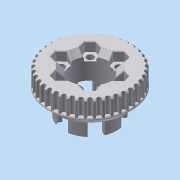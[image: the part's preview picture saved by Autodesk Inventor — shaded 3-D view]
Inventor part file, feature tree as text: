
AUTODESK INVENTOR PART (.ipt)
format: ipt  version: 2014 SP1 (Build 180222100, 222)  size: 2,198,528 bytes
history: native  units: in
note: dims shown in document units (in); Inventor stores cm internally (conversion verified against a paired STEP export)
features: extrude x7, other x4, sketch x4, fillet x4, chamfer x3, projected_geometry x2, move_body x1
ambient origin geometry x8: Origin, YZ Plane, XZ Plane, XY Plane, X Axis, Y Axis, Z Axis, Center Point
bodies: Solid1 (feature_tree), Solid3 (feature_tree)
feature tree (25):
  other  "wheelinsertsketch.ipt"
  other  "40t_pulley.ipt"
  extrude  "Extrusion1"  Depth=0.5in TaperAngle=0.0deg
  extrude  "Extrusion2"  Depth=0.3in TaperAngle=0.0deg
  chamfer  "Chamfer1"  Distance=0.25in Angle=45.0deg
  sketch  "Sketch14"  dims[d39=1.1in d40=0.4724in d41=0.0in d42=5.0in d43=0.0in d44=0.05in d45=0.02in d46=0.125in d61=0.1625in d62=0.125in d63=45.0deg d80=0.38in d81=2.3622in d83=360.0deg d85=1.0in d86=0.0in d87=0.2756in d88=0.0in d90=0.4724in d91=0.0in d92=0.0591in d93=0.125in d94=45.0deg d96=0.0394in d102=0.205in d103=0.0787in]
  move_body  "Move Body2"
  extrude  "Extrusion14"  TaperAngle=90.0deg  [1 undecoded]
  chamfer  "Chamfer7"  Distance=0.4724in
  fillet  "Fillet21"  Radius=5.0in
  extrude  "Extrusion6"  Depth=0.05in
  extrude  "hella sketch"  Depth=0.02in
  fillet  "Fillet6"  Radius=0.125in
  fillet  "Fillet7"  Radius=0.1625in
  chamfer  "Chamfer4"  Distance=0.38in
  sketch  "Sketch12"  dims[d3=2.4803in d4=0.3in d5=0.0in d6=0.25in d7=0.125in d8=45.0deg]
  extrude  "Extrusion12"  Depth=2.3622in TaperAngle=360.0deg
  extrude  "Extrusion13"  Depth=1.0in TaperAngle=0.0deg
  fillet  "Fillet18"  Radius=0.2756in
  other  "Solid1::40t_pulley.ipt"
  other  "TaggingFeature2"
  projected_geometry  "Projected Loop2"
  sketch  "Sketch7"  dims[d0=0.3937in d1=0.5in d2=0.0in]
  sketch  "Sketch13"  dims[d34=0.3937in d35=90.0deg d36=0.0in d37=-2.0in d38=0.0in]
  projected_geometry  "Projected Loop4"
note: 1 required parameter value undecoded (feature->parameter linkage not recoverable at this tier; creation-order binding heuristic only, values carry confidence <= 0.55)
